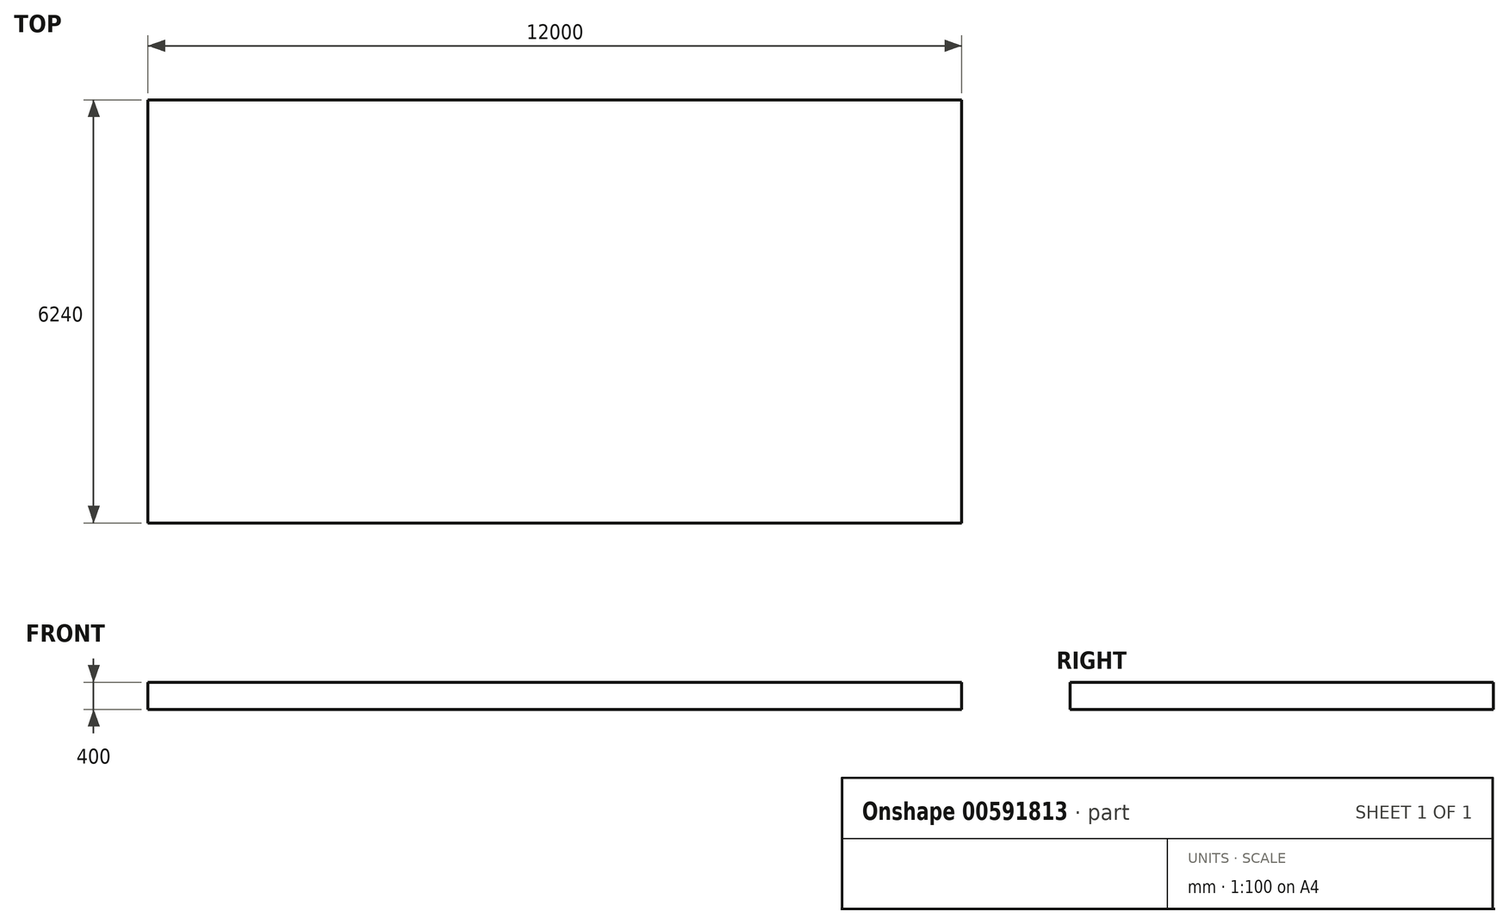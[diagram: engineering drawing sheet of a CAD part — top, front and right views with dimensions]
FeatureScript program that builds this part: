
annotation { "Feature Type Name" : "Feature", "Feature Type Description" : "" }
export const myFeature = defineFeature(function(context is Context, id is Id, definition is map)
    precondition{}
    {
        {
            var Q0;
            Q0=qCreatedBy(makeId("Top.planeOp"),FACE);
            var sketch = newSketch(context, id + "F0", { "sketchPlane" : qUnion([Q0])});
            skLineSegment(sketch, "E0.bottom", {"start": v(0, 0) * mm, "end": v(12000, 0) * mm});
            skLineSegment(sketch, "E0.top", {"start": v(0, -6240) * mm, "end": v(12000, -6240) * mm});
            skLineSegment(sketch, "E0.left", {"start": v(0, 0) * mm, "end": v(0, -6240) * mm});
            skLineSegment(sketch, "E0.right", {"start": v(12000, 0) * mm, "end": v(12000, -6240) * mm});
            skSolve(sketch);
        }
        {
            var Q0;
            Q0=makeQuery(id+"F0.imprint","IMPRINT",FACE,{"disambiguationData":[TD([[makeQuery(id+"F0.imprint","IMPRINT",EDGE,{"derivedFrom":sQuery(id+"F0.wireOp",EDGE,"E0.bottom")}),-1.0]])]});
            extrude(context, id + "F1", {"entities" : qUnion([Q0]), "depth" : 400 * mm, "offsetDistance" : 25 * mm});
        }
    });
